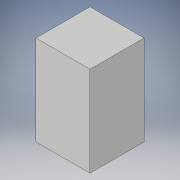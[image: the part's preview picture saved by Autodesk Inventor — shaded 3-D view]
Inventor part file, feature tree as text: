
AUTODESK INVENTOR PART (.ipt)
format: ipt  version: 2019.4 (Build 234330000, 330)  size: 86,528 bytes
history: native  units: in
note: dims shown in document units (in); Inventor stores cm internally (conversion verified against a paired STEP export)
features: extrude x1, sketch x1
ambient origin geometry x8: Origin, YZ Plane, XZ Plane, XY Plane, X Axis, Y Axis, Z Axis, Center Point
bodies: Solid1 (feature_tree)
feature tree (2):
  extrude  "Extrusion1"  Depth=0.2362in
  sketch  "Sketch1"  dims[d0=0.2362in d1=0.2362in d2=0.3937in d3=0.0in]
